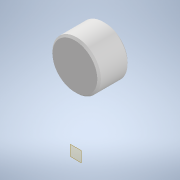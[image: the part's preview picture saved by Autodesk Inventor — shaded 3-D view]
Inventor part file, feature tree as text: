
AUTODESK INVENTOR PART (.ipt)
format: ipt  version: 2021 (Build 250183000, 183)  size: 111,616 bytes
history: native  units: mm
features: other x5, extrude x1, chamfer x1, reference x1
ambient origin geometry x8: Origin, YZ Plane, XZ Plane, XY Plane, X Axis, Y Axis, Z Axis, Center Point
bodies: Body1 (feature_tree)
feature tree (8):
  other  "Bryła1"
  other  "Płaszczyzna konstrukcyjna1"
  extrude  "Wyciągnięcie proste1"  Depth=80.0mm
  chamfer  "Faza1"  Distance=50.0mm
  reference  "Odniesienie1"
  other  "cw12model.iam"
  other  "shaft:1"
  other  "rurka:2"
